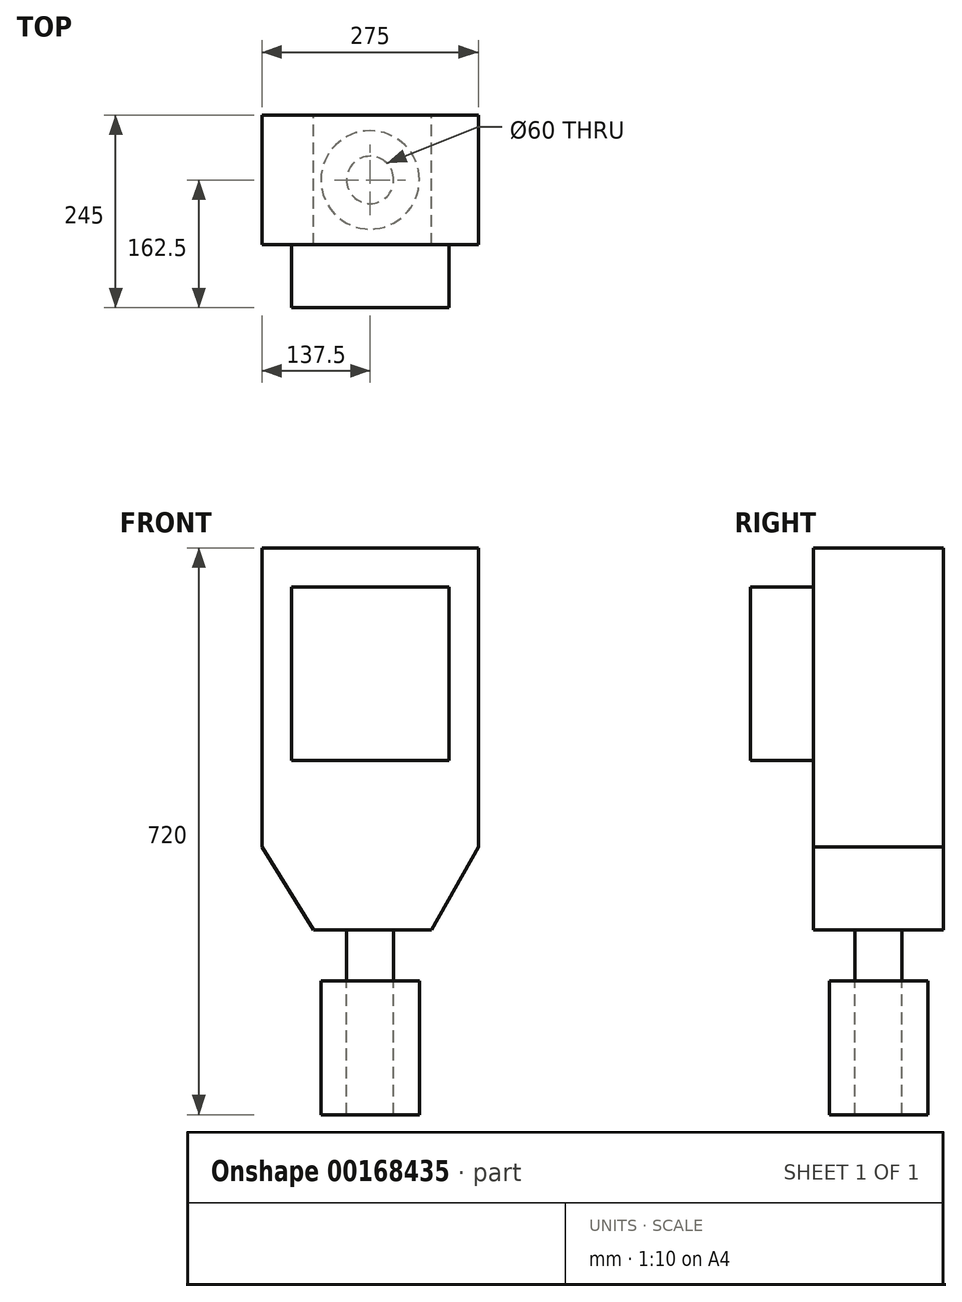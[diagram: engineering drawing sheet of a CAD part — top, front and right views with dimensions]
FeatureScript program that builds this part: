
annotation { "Feature Type Name" : "Feature", "Feature Type Description" : "" }
export const myFeature = defineFeature(function(context is Context, id is Id, definition is map)
    precondition{}
    {
        {
            var Q0;
            Q0=qCreatedBy(makeId("Front.planeOp"),FACE);
            var sketch = newSketch(context, id + "F0", { "sketchPlane" : qUnion([Q0])});
            skLineSegment(sketch, "E0.bottom", {"start": v(137.5, 190) * mm, "end": v(-137.5, 190) * mm});
            skLineSegment(sketch, "E0.left", {"start": v(137.5, 190) * mm, "end": v(137.5, -190) * mm});
            skLineSegment(sketch, "E0.right", {"start": v(-137.5, 190) * mm, "end": v(-137.5, -190) * mm});
            skPoint(sketch, "E0.middle", {"position": v(0, 0) * mm});
            skLineSegment(sketch, "E1", {"start": v(-72.01, -295) * mm, "end": v(77.99, -295) * mm});
            skLineSegment(sketch, "E2", {"start": v(-72.01, -295) * mm, "end": v(-137.5, -190) * mm});
            skLineSegment(sketch, "E3", {"start": v(77.99, -295) * mm, "end": v(137.5, -190) * mm});
            skPoint(sketch, "E4.end.orphan", {"position": v(2.99, -295) * mm});
            skSolve(sketch);
        }
        {
            var Q0;
            Q0=makeQuery(id+"F0.imprint","IMPRINT",FACE,{"disambiguationData":[TD([[makeQuery(id+"F0.imprint","IMPRINT",EDGE,{"derivedFrom":sQuery(id+"F0.wireOp",EDGE,"E0.bottom")}),1.0]])]});
            extrude(context, id + "F1", {"entities" : qUnion([Q0]), "depth" : 165 * mm});
        }
        {
            var Q0;
            Q0=makeQuery(id+"F1.opExtrude","SWEPT_FACE",FACE,{"disambiguationData":[OSD([sQuery(id+"F0.wireOp",EDGE,"E1")])]});
            var sketch = newSketch(context, id + "F7", { "sketchPlane" : qUnion([Q0])});
            skPoint(sketch, "E5", {"position": v(77.99, 82.5) * mm});
            skCircle(sketch, "E6", {"center": v(0, 82.5) * mm, "radius": 30 * mm});
            skSolve(sketch);
        }
        {
            var Q0;
            Q0=makeQuery(id+"F7.imprint","IMPRINT",FACE,{"disambiguationData":[TD([[makeQuery(id+"F7.imprint","IMPRINT",EDGE,{"derivedFrom":sQuery(id+"F7.wireOp",EDGE,"E6")}),1.0]])]});
            extrude(context, id + "F2", {"entities" : qUnion([Q0]), "operationType" : NewBodyOperationType.ADD, "depth" : 65 * mm});
        }
        {
            var Q0;
            Q0=makeQuery(id+"F2.opExtrude","CAP_FACE",FACE,{"disambiguationData":[OSD([sQuery(id+"F7.wireOp",EDGE,"E6")])],"isStart":false});
            var sketch = newSketch(context, id + "F3", { "sketchPlane" : qUnion([Q0])});
            skCircle(sketch, "E7", {"center": v(0, 82.5) * mm, "radius": 62.5 * mm});
            skSolve(sketch);
        }
        {
            var Q0;
            Q0=makeQuery(id+"F3.imprint","IMPRINT",FACE,{"disambiguationData":[TD([[makeQuery(id+"F3.imprint","IMPRINT",EDGE,{"derivedFrom":sQuery(id+"F3.wireOp",EDGE,"E7")}),1.0]])]});
            extrude(context, id + "F4", {"entities" : qUnion([Q0]), "operationType" : NewBodyOperationType.ADD, "depth" : 170 * mm});
        }
        {
            var Q0;
            Q0=makeQuery(id+"F1.opExtrude","CAP_FACE",FACE,{"disambiguationData":[OSD([sQuery(id+"F0.wireOp",EDGE,"E0.bottom"),sQuery(id+"F0.wireOp",EDGE,"E0.left"),sQuery(id+"F0.wireOp",EDGE,"E0.right"),sQuery(id+"F0.wireOp",EDGE,"E1"),sQuery(id+"F0.wireOp",EDGE,"E2"),sQuery(id+"F0.wireOp",EDGE,"E3")])],"isStart":false});
            var sketch = newSketch(context, id + "F5", { "sketchPlane" : qUnion([Q0])});
            skLineSegment(sketch, "E8.bottom", {"start": v(100, 140) * mm, "end": v(-100, 140) * mm});
            skLineSegment(sketch, "E8.top", {"start": v(100, -80) * mm, "end": v(-100, -80) * mm});
            skLineSegment(sketch, "E8.left", {"start": v(100, 140) * mm, "end": v(100, -80) * mm});
            skLineSegment(sketch, "E8.right", {"start": v(-100, 140) * mm, "end": v(-100, -80) * mm});
            skPoint(sketch, "E8.middle", {"position": v(0, 30) * mm});
            skSolve(sketch);
        }
        {
            var Q0;
            Q0=makeQuery(id+"F5.imprint","IMPRINT",FACE,{"disambiguationData":[TD([[makeQuery(id+"F5.imprint","IMPRINT",EDGE,{"derivedFrom":sQuery(id+"F5.wireOp",EDGE,"E8.bottom")}),1.0]])]});
            extrude(context, id + "F6", {"entities" : qUnion([Q0]), "operationType" : NewBodyOperationType.ADD, "depth" : 80 * mm});
        }
    });
